# Revit family: G-2021_ES_Caldera_De-Dietrich_Inidens
name_source: partatom
category: Mechanical Equipment
units: mm (PartAtom-declared; Revit-internal decimal feet)

## family parameters
Always vertical = Yes
Cut with Voids When Loaded = No
Host = Wall
OmniClass Number = 23.65.35.11
OmniClass Title = Supply Water Heaters
Part Type = Normal
Room Calculation Point = No
Round Connector Dimension = Use Diameter
Shared = No

## types (4) — shared parameters
Altura = 776 mm  [stored 2.54593 ft]
Altura minima requerida = 1200 mm  [stored 3.93701 ft]
Anchura = 395 mm  [stored 1.29593 ft]
Autor = De Dietrich Thermique Iberia, S.L.U.
COBie Categoria = IfcBoiler
Calificacion de presion = 100.0 Pa
Caudal ACS = 0.0 L/s
Codigo = INIDENS 24
Description = Calderas murales de condensación de gas completamente preajustadas, equipadas para funcionar con gas natural o propano.
Diámetro Desagüe Válvula Seguridad = 13 mm
Diámetro Desagüe de Condensados = 13 mm
Diámetro Entrada Agua Fría = 13 mm
Diámetro Impulsión Calefacción = 19 mm
Diámetro Retorno Calefacción = 13 mm
Diámetro Salida ACS = 13 mm
Es Accesible = Yes
Es Exterior = No
Es calentador de almacenamiento de agua = Yes
Etiqueta Modelo = INIDENS 24
Fecha Emision Elemento BIM = 25.05.2022
Fecha Vencimiento Elemento BIM = 25.05.2023
Fuente de energia = gas natural o propano
Garantia Extendida = Yes
Gubimclass Codigo = 50.30.10.40
Gubimclass Titulo = Calderas
Historial = (RVT2021) Creación de Elemento.
IfcExportAs = IfcBoiler
IfcExportType = Caldera
Informacion Tecnica = https://www.dedietrich-calefaccion.es
Manufacturer = De Dietrich Thermique Iberia, S.L.U.
Marcado CE = No
Masterformat Codigo = 23 52 00
Masterformat Titulo = Heating Boilers
Material = Latón, pintado blanco
Model = INIDENS 24
Numero de Licencia = XXX-XXXX7125
Omniclass Codigo = 23-33 11 00
Omniclass Titulo = Commercial Boilers
Peso = 0.00 kg
Plataforma descaga contenido BIM = www.bimetica.com
Profundidad = 285 mm  [stored 0.935039 ft]
Rango de temperatura de salida = de 25 a 80 °C
Rango de temperatura de suministro de agua = de 35 a 60 °C
Referencia = INIDENS
Serie = INIDENS
Soporte tecnico BIM = https://bimsupport.info
Titular = De Dietrich Thermique Iberia, S.L.U.
UNSPSC Codigo = 40102000
UNSPSC Titulo = Boilers
URL = www.dedietrich-calefaccion.es
URL Perfil BIM = https://bimetica.com
URL Producto = https://www.dedietrich-calefaccion.es
Uniclass2015 Codigo = Pr_60-60-08
Uniclass2015 Titulo = Boilers
Unidad Medicion = Unidad
Version = RVT2021
Version Estandar GDO-BIM = GDO-BIM V02
zero-valued in all types: Acidificacion Atmosferica por Unidad, Agua Consumida por Unidad, Cambio Climatico por Unidad, Capacidad de almacenamiento de agua, Coste Mantenimiento, Curvas de eficiencia de carga parcial, Default Elevation, Desfase, Destruccion Capa Ozono Estratosferica por Unidad, Energia No Renovable Consumida por Unidad, Energia Primaria Total Consumida por Unidad, Energia Renovable Consumida por Unidad, Energia consumida, Espacio libre acceso, Eutrofizacion por Unidad, Falta de Recursos por Unidad, Formacion Fotoquimica Ozono por Unidad, Relacion de carga parcial nominal, Residuo Inerte por Unidad, Residuo Radioactivo por Unidad, Residuos No Peligrosos por Unidad, Residuos Peligrosos por Unidad, Área de Superficie de Transferencia de Calor

## per-type parameters (varying)
| type | Consumo nominal de energia | Diámetro Salida Gases Combustión |
| INIDENS 24 | 24000 W | 610 mm |
| INIDENS 20/24 MI | 20000 W | 610 mm |
| INIDENS 24/28 MI | 24000 W | 610 mm |
| INIDENS 30/35 MI | 30000 W | 100 mm  [stored 0.328084 ft] |

note: [stored X ft] marks values corroborated as IEEE doubles in the binary element streams (Revit-internal decimal feet)

## geometry (parser evidence)
native form markers: Sweep x3
no freeform markers — native parametric forms only
